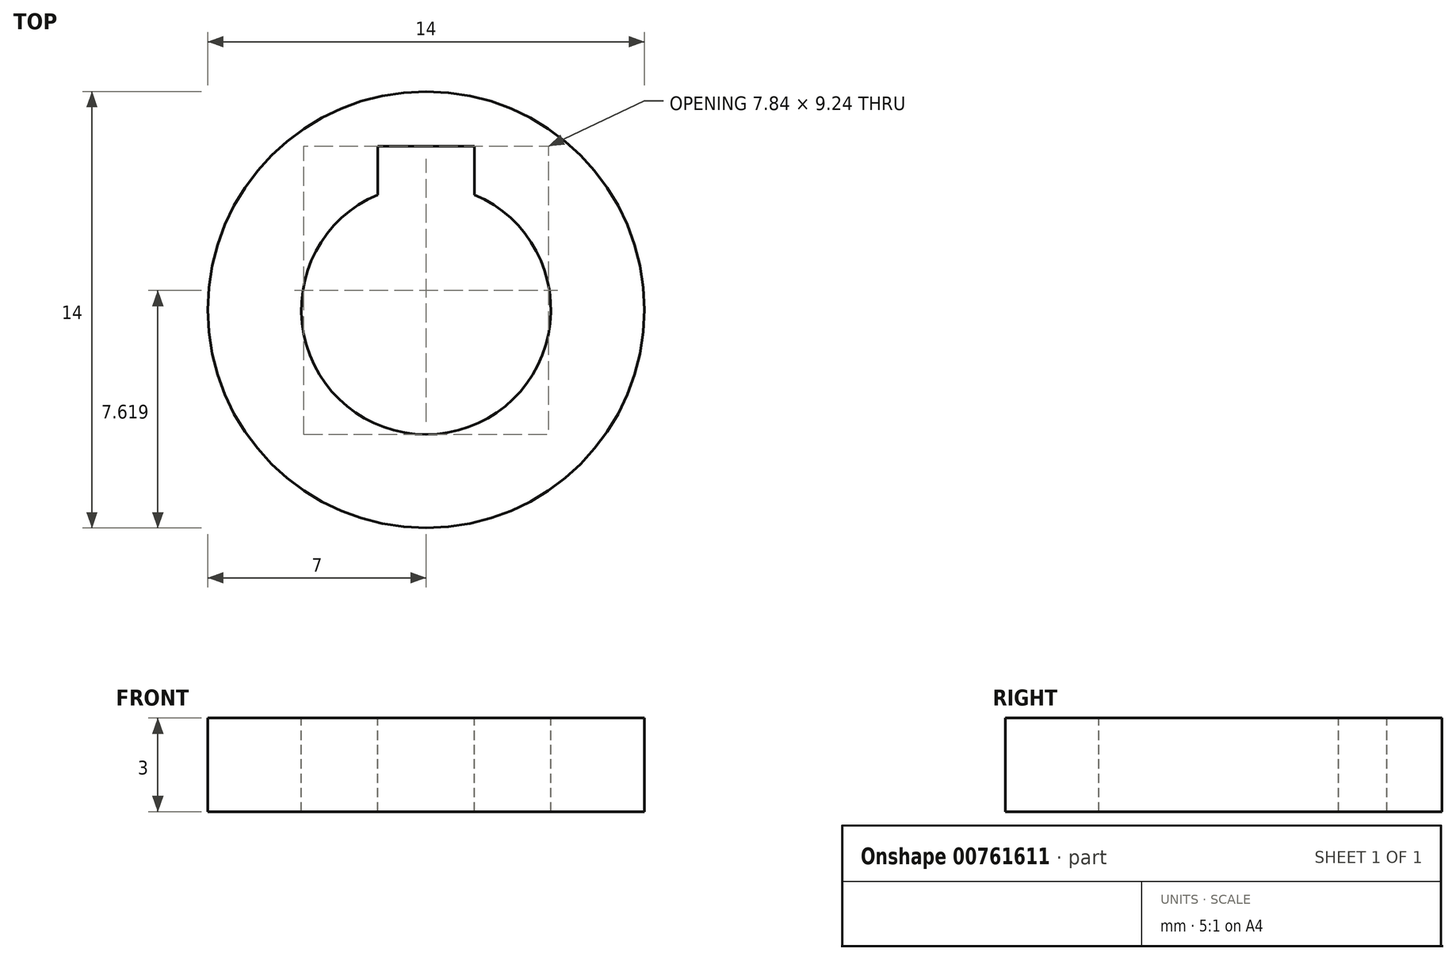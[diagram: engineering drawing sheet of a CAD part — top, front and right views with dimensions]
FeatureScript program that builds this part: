
annotation { "Feature Type Name" : "Feature", "Feature Type Description" : "" }
export const myFeature = defineFeature(function(context is Context, id is Id, definition is map)
    precondition{}
    {
        {
            var Q0;
            Q0=qCreatedBy(makeId("Top.planeOp"),FACE);
            var sketch = newSketch(context, id + "F0", { "sketchPlane" : qUnion([Q0])});
            skCircle(sketch, "E0", {"center": v(0, 0) * mm, "radius": 7 * mm});
            skSolve(sketch);
        }
        {
            var Q0;
            Q0 = qSketchRegion(id + "F0", true);
            extrude(context, id + "F1", {"entities" : qUnion([Q0]), "depth" : 3 * mm, "offsetDistance" : 25 * mm});
        }
        {
            var Q0;
            Q0=makeQuery(id+"F1.opExtrude","CAP_FACE",FACE,{"disambiguationData":[OSD([sQuery(id+"F0.wireOp",EDGE,"E0")])],"isStart":false});
            var sketch = newSketch(context, id + "F2", { "sketchPlane" : qUnion([Q0])});
            skCircle(sketch, "E1", {"center": v(0, 0) * mm, "radius": 4 * mm});
            skLineSegment(sketch, "E2", {"start": v(0, 4) * mm, "end": v(0, 5.24) * mm, "construction": true});
            skLineSegment(sketch, "E3", {"start": v(0, 5.24) * mm, "end": v(1.55, 5.24) * mm});
            skLineSegment(sketch, "E4", {"start": v(1.55, 5.24) * mm, "end": v(1.55, 3.69) * mm});
            skLineSegment(sketch, "E5.MirrorCS", {"start": v(0, 5.24) * mm, "end": v(-1.55, 5.24) * mm});
            skLineSegment(sketch, "E6.MirrorCS", {"start": v(-1.55, 5.24) * mm, "end": v(-1.55, 3.69) * mm});
            skSolve(sketch);
        }
        {
            var Q0;
            Q0 = qSketchRegion(id + "F2", true);
            var Q1;
            Q1=makeQuery(id+"F1.opExtrude","CAP_FACE",FACE,{"disambiguationData":[OSD([sQuery(id+"F0.wireOp",EDGE,"E0")])],"isStart":true});
            extrude(context, id + "F3", {"entities" : qUnion([Q0]), "operationType" : NewBodyOperationType.REMOVE, "endBound" : BoundingType.UP_TO_SURFACE, "oppositeDirection" : true, "depth" : 25 * mm, "endBoundEntityFace" : qUnion([Q1]), "offsetDistance" : 25 * mm});
        }
    });
